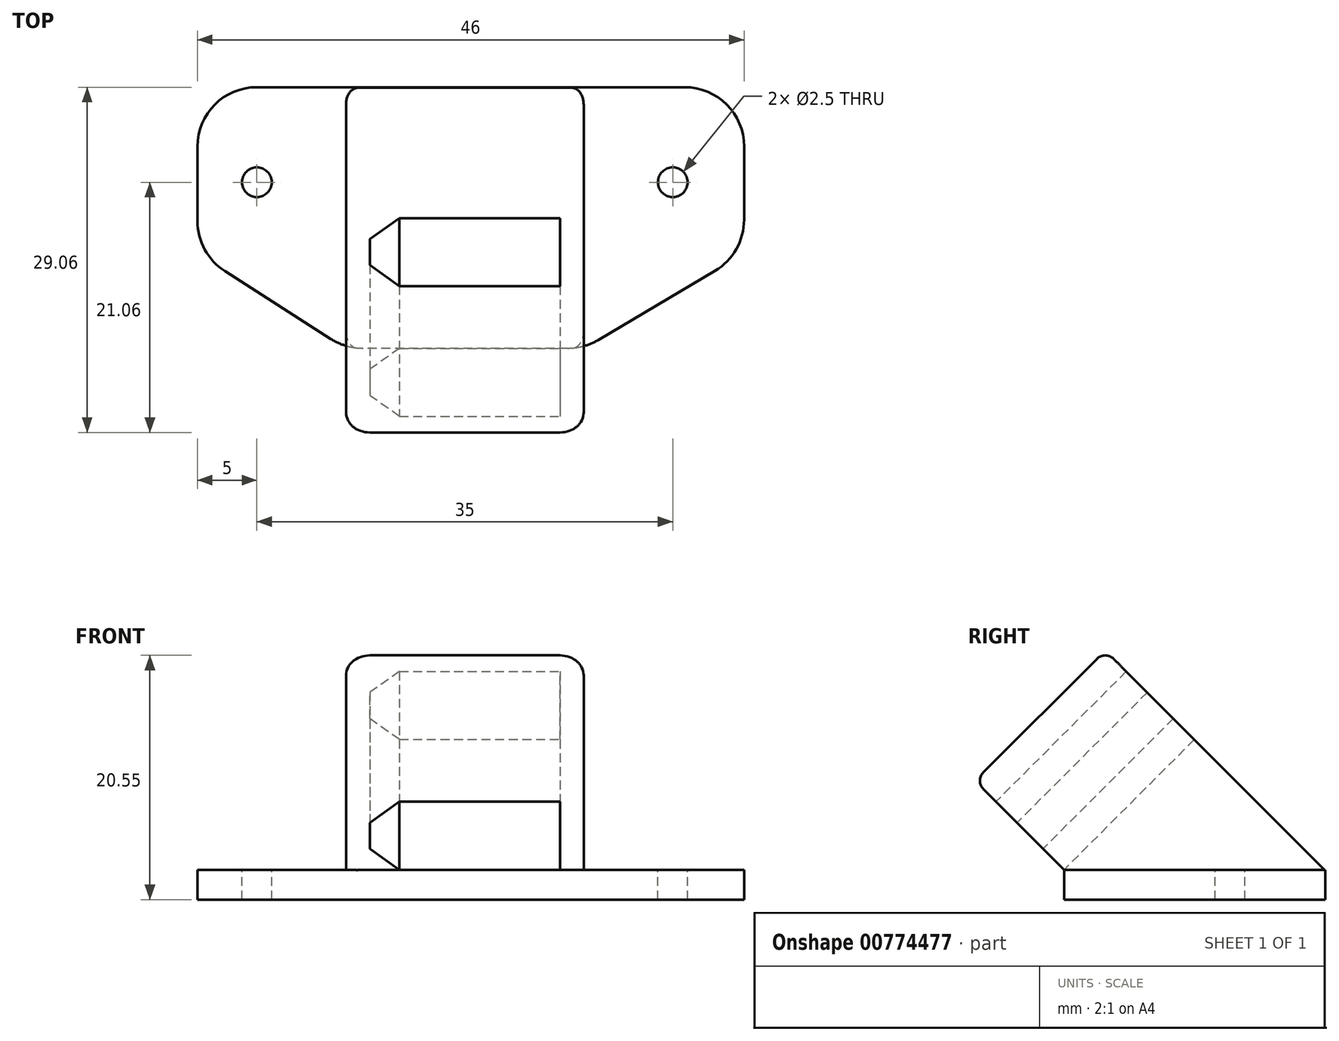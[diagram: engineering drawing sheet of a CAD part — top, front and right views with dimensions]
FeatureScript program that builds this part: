
annotation { "Feature Type Name" : "Feature", "Feature Type Description" : "" }
export const myFeature = defineFeature(function(context is Context, id is Id, definition is map)
    precondition{}
    {
        {
            var Q0;
            Q0=qCreatedBy(makeId("Top.planeOp"),FACE);
            var sketch = newSketch(context, id + "F0", { "sketchPlane" : qUnion([Q0])});
            skLineSegment(sketch, "E0.bottom", {"start": v(-22.5, -7.5) * mm, "end": v(23.5, -7.5) * mm});
            skLineSegment(sketch, "E0.top", {"start": v(-22.5, -29.5) * mm, "end": v(23.5, -29.5) * mm});
            skLineSegment(sketch, "E0.left", {"start": v(-22.5, -7.5) * mm, "end": v(-22.5, -29.5) * mm});
            skLineSegment(sketch, "E0.right", {"start": v(23.5, -7.5) * mm, "end": v(23.5, -29.5) * mm});
            skCircle(sketch, "E1", {"center": v(-17.5, -15.5) * mm, "radius": 1.25 * mm});
            skPoint(sketch, "E1.centerSnap0", {"position": v(-22.5, -15.5) * mm});
            skCircle(sketch, "E2.MirrorC", {"center": v(17.5, -15.5) * mm, "radius": 1.25 * mm});
            skLineSegment(sketch, "E3", {"start": v(-22.5, -21.5) * mm, "end": v(-10, -29.5) * mm});
            skLineSegment(sketch, "E4", {"start": v(23.5, -21.5) * mm, "end": v(10, -29.5) * mm});
            skSolve(sketch);
        }
        {
            var Q0;
            Q0=makeQuery(id+"F0.imprint","IMPRINT",FACE,{"disambiguationData":[TD([[makeQuery(id+"F0.imprint","IMPRINT",EDGE,{"derivedFrom":sQuery(id+"F0.wireOp",EDGE,"E0.bottom")}),-1.0]])]});
            extrude(context, id + "F1", {"entities" : qUnion([Q0]), "oppositeDirection" : true, "depth" : 2.5 * mm, "offsetDistance" : 25 * mm});
        }
        {
            var Q0;
            Q0=qCreatedBy(makeId("Top.planeOp"),FACE);
            var sketch = newSketch(context, id + "F2", { "sketchPlane" : qUnion([Q0])});
            skLineSegment(sketch, "E5.bottom", {"start": v(-10, 0) * mm, "end": v(10, 0) * mm});
            skLineSegment(sketch, "E5.top", {"start": v(-10, 15.5) * mm, "end": v(10, 15.5) * mm});
            skLineSegment(sketch, "E5.left", {"start": v(-10, 0) * mm, "end": v(-10, 15.5) * mm});
            skLineSegment(sketch, "E5.right", {"start": v(10, 0) * mm, "end": v(10, 15.5) * mm});
            skSolve(sketch);
        }
        {
            var Q0;
            Q0 = qSketchRegion(id + "F2", true);
            extrude(context, id + "F3", {"entities" : qUnion([Q0]), "operationType" : NewBodyOperationType.ADD, "depth" : 27 * mm, "offsetDistance" : 25 * mm});
        }
        {
            var Q0;
            Q0=makeQuery(id+"F3.opExtrude","SWEPT_FACE",FACE,{"disambiguationData":[OSD([sQuery(id+"F2.wireOp",EDGE,"E5.bottom")])]});
            var sketch = newSketch(context, id + "F4", { "sketchPlane" : qUnion([Q0])});
            skLineSegment(sketch, "E6.bottom", {"start": v(-8, 24.5) * mm, "end": v(8, 24.5) * mm});
            skLineSegment(sketch, "E6.top", {"start": v(-8, 16.4) * mm, "end": v(8, 16.4) * mm});
            skLineSegment(sketch, "E6.left", {"start": v(8, 16.4) * mm, "end": v(8, 24.5) * mm});
            skLineSegment(sketch, "E6.right", {"start": v(-8, 16.4) * mm, "end": v(-8, 24.5) * mm});
            skLineSegment(sketch, "E7", {"start": v(-5.5, 24.5) * mm, "end": v(-8, 22) * mm});
            skLineSegment(sketch, "E8", {"start": v(-5.5, 16.4) * mm, "end": v(-8, 18.9) * mm});
            skSolve(sketch);
        }
        {
            var Q0;
            {var subQ3=sQuery(id+"F4.wireOp",EDGE,"E6.left");Q0=makeQuery(id+"F4.imprint","IMPRINT",FACE,{"disambiguationData":[TD([[makeQuery(id+"F4.imprint","IMPRINT",EDGE,{"derivedFrom":subQ3}),1.0]])]});}
            var Q1;
            Q1=makeQuery(id+"F3.opExtrude","SWEPT_FACE",FACE,{"disambiguationData":[OSD([sQuery(id+"F2.wireOp",EDGE,"E5.top")])]});
            extrude(context, id + "F5", {"entities" : qUnion([Q0]), "operationType" : NewBodyOperationType.REMOVE, "endBound" : BoundingType.UP_TO_SURFACE, "oppositeDirection" : true, "depth" : 25 * mm, "endBoundEntityFace" : qUnion([Q1]), "offsetDistance" : 25 * mm});
        }
        {
            var Q0;
            Q0=qCreatedBy(makeId("Top.planeOp"),FACE);
            var sketch = newSketch(context, id + "F6", { "sketchPlane" : qUnion([Q0])});
            skLineSegment(sketch, "E9", {"start": v(-27.41, 0) * mm, "end": v(24.32, 0) * mm, "construction": true});
            skSolve(sketch);
        }
        {
            var Q0;
            Q0=makeQuery(id+"F3.opExtrude","SWEPT_BODY",BODY,{"disambiguationData":[OSD([sQuery(id+"F2.wireOp",EDGE,"E5.bottom"),sQuery(id+"F2.wireOp",EDGE,"E5.top"),sQuery(id+"F2.wireOp",EDGE,"E5.left"),sQuery(id+"F2.wireOp",EDGE,"E5.right")])]});
            var Q1;
            Q1=sQuery(id+"F6.wireOp",EDGE,"E9");
            transform(context, id + "F7", {"entities" : qUnion([Q0]), "transformType" : TransformType.ROTATION, "transformAxis" : qUnion([Q1]), "angle" : 45 * degree, "makeCopy" : false});
        }
        {
            var Q0;
            Q0=makeQuery(id+"F3.opExtrude","SWEPT_BODY",BODY,{"disambiguationData":[OSD([sQuery(id+"F2.wireOp",EDGE,"E5.bottom"),sQuery(id+"F2.wireOp",EDGE,"E5.top"),sQuery(id+"F2.wireOp",EDGE,"E5.left"),sQuery(id+"F2.wireOp",EDGE,"E5.right")])]});
            transform(context, id + "F8", {"entities" : qUnion([Q0]), "transformType" : TransformType.TRANSLATION_3D, "dx" : 0 * mm, "dy" : -17.88 * mm, "dz" : -11.6 * mm, "makeCopy" : false});
        }
        {
            var Q0;
            Q0=makeQuery(id+"F1.opExtrude","SWEPT_BODY",BODY,{"disambiguationData":[OSD([sQuery(id+"F0.wireOp",EDGE,"E0.bottom"),sQuery(id+"F0.wireOp",EDGE,"E0.top"),sQuery(id+"F0.wireOp",EDGE,"E0.left"),sQuery(id+"F0.wireOp",EDGE,"E0.right"),sQuery(id+"F0.wireOp",EDGE,"E1"),sQuery(id+"F0.wireOp",EDGE,"E2.MirrorC")])]});
            var Q1;
            Q1=makeQuery(id+"F3.opExtrude","SWEPT_BODY",BODY,{"disambiguationData":[OSD([sQuery(id+"F2.wireOp",EDGE,"E5.bottom"),sQuery(id+"F2.wireOp",EDGE,"E5.top"),sQuery(id+"F2.wireOp",EDGE,"E5.left"),sQuery(id+"F2.wireOp",EDGE,"E5.right")])]});
            booleanBodies(context, id + "F9", {"operationType" : BooleanOperationType.UNION, "tools" : qUnion([Q0, Q1])});
        }
        {
            var Q0;
            Q0=qCreatedBy(makeId("Right.planeOp"),FACE);
            var sketch = newSketch(context, id + "F10", { "sketchPlane" : qUnion([Q0])});
            skLineSegment(sketch, "E10", {"start": v(-36.97, 7.5) * mm, "end": v(-29.47, 0) * mm});
            skLineSegment(sketch, "E11", {"start": v(-29.47, -2.5) * mm, "end": v(-7.5, -2.5) * mm});
            skLineSegment(sketch, "E12", {"start": v(-7.5, -2.5) * mm, "end": v(-7.5, 0) * mm});
            skLineSegment(sketch, "E13", {"start": v(-7.5, 0) * mm, "end": v(-5.54, 0) * mm});
            skLineSegment(sketch, "E14", {"start": v(-5.54, 0) * mm, "end": v(-5.54, -13.55) * mm});
            skLineSegment(sketch, "E15", {"start": v(-5.54, -13.55) * mm, "end": v(-36.97, -13.55) * mm});
            skLineSegment(sketch, "E16", {"start": v(-36.97, -13.55) * mm, "end": v(-36.97, 7.5) * mm});
            skLineSegment(sketch, "E17", {"start": v(-29.47, 0) * mm, "end": v(-29.47, -2.5) * mm});
            skSolve(sketch);
        }
        {
            var Q0;
            Q0=makeQuery(id+"F10.imprint","IMPRINT",FACE,{"disambiguationData":[TD([[makeQuery(id+"F10.imprint","IMPRINT",EDGE,{"derivedFrom":sQuery(id+"F10.wireOp",EDGE,"E10")}),-1.0]])]});
            extrude(context, id + "F11", {"entities" : qUnion([Q0]), "operationType" : NewBodyOperationType.REMOVE, "endBound" : BoundingType.SYMMETRIC, "depth" : 50 * mm, "offsetDistance" : 25 * mm});
        }
        {
            var Q0;
            Q0=makeQuery(id+"F3.opExtrude","CAP_EDGE",EDGE,{"disambiguationData":[OSD([sQuery(id+"F2.wireOp",EDGE,"E5.left")])],"isStart":false});
            var Q1;
            Q1=makeQuery(id+"F3.opExtrude","CAP_EDGE",EDGE,{"disambiguationData":[OSD([sQuery(id+"F2.wireOp",EDGE,"E5.right")])],"isStart":false});
            fillet(context, id + "F12", {"entities" : qUnion([Q0, Q1]), "radius" : 2 * mm, "tangentPropagation" : true, "allowEdgeOverflow" : false});
        }
        {
            var Q0;
            {var subQ0=sQuery(id+"F2.wireOp",EDGE,"E5.top");var subQ1=sQuery(id+"F2.wireOp",EDGE,"E5.left");Q0=makeQuery(id+"F9.opBoolean","SPLIT",EDGE,{"disambiguationData":[TD([makeQuery(id+"F3.opExtrude","CAP_FACE",FACE,{"disambiguationData":[OSD([sQuery(id+"F2.wireOp",EDGE,"E5.bottom"),subQ0,subQ1,sQuery(id+"F2.wireOp",EDGE,"E5.right")])],"isStart":false})])],"derivedFrom":makeQuery(id+"F3.opExtrude","SWEPT_EDGE",EDGE,{"disambiguationData":[OSD([subQ0,subQ1])]})});}
            var Q1;
            Q1=makeQuery(id+"F3.opExtrude","CAP_EDGE",EDGE,{"disambiguationData":[OSD([sQuery(id+"F2.wireOp",EDGE,"E5.top")])],"isStart":false});
            var Q2;
            {var subQ0=sQuery(id+"F2.wireOp",EDGE,"E5.top");var subQ1=sQuery(id+"F2.wireOp",EDGE,"E5.right");Q2=makeQuery(id+"F9.opBoolean","SPLIT",EDGE,{"disambiguationData":[TD([makeQuery(id+"F3.opExtrude","CAP_FACE",FACE,{"disambiguationData":[OSD([sQuery(id+"F2.wireOp",EDGE,"E5.bottom"),subQ0,sQuery(id+"F2.wireOp",EDGE,"E5.left"),subQ1])],"isStart":false})])],"derivedFrom":makeQuery(id+"F3.opExtrude","SWEPT_EDGE",EDGE,{"disambiguationData":[OSD([subQ0,subQ1])]})});}
            var Q3;
            Q3=makeQuery(id+"F3.opExtrude","CAP_EDGE",EDGE,{"disambiguationData":[OSD([sQuery(id+"F2.wireOp",EDGE,"E5.bottom")])],"isStart":false});
            fillet(context, id + "F13", {"entities" : qUnion([Q0, Q1, Q2, Q3]), "radius" : 1 * mm, "tangentPropagation" : true, "allowEdgeOverflow" : false});
        }
        {
            var Q0;
            Q0=makeQuery(id+"F1.opExtrude","SWEPT_EDGE",EDGE,{"disambiguationData":[OSD([sQuery(id+"F0.wireOp",EDGE,"E0.left"),sQuery(id+"F0.wireOp",EDGE,"E3")])]});
            var Q1;
            Q1=makeQuery(id+"F1.opExtrude","SWEPT_EDGE",EDGE,{"disambiguationData":[OSD([sQuery(id+"F0.wireOp",EDGE,"E0.bottom"),sQuery(id+"F0.wireOp",EDGE,"E0.left")])]});
            var Q2;
            Q2=makeQuery(id+"F1.opExtrude","SWEPT_EDGE",EDGE,{"disambiguationData":[OSD([sQuery(id+"F0.wireOp",EDGE,"E0.bottom"),sQuery(id+"F0.wireOp",EDGE,"E0.right")])]});
            var Q3;
            Q3=makeQuery(id+"F1.opExtrude","SWEPT_EDGE",EDGE,{"disambiguationData":[OSD([sQuery(id+"F0.wireOp",EDGE,"E0.right"),sQuery(id+"F0.wireOp",EDGE,"E4")])]});
            var Q4;
            Q4=makeQuery(id+"F11.boolean.opBoolean","INTERSECT",EDGE,{"derivedFrom":[makeQuery(id+"F1.opExtrude","SWEPT_FACE",FACE,{"disambiguationData":[OSD([sQuery(id+"F0.wireOp",EDGE,"E3")])]}),makeQuery(id+"F11.opExtrude","SWEPT_FACE",FACE,{"disambiguationData":[OSD([sQuery(id+"F10.wireOp",EDGE,"E17")])]})]});
            var Q5;
            Q5=makeQuery(id+"F11.boolean.opBoolean","INTERSECT",EDGE,{"derivedFrom":[makeQuery(id+"F1.opExtrude","SWEPT_FACE",FACE,{"disambiguationData":[OSD([sQuery(id+"F0.wireOp",EDGE,"E4")])]}),makeQuery(id+"F11.opExtrude","SWEPT_FACE",FACE,{"disambiguationData":[OSD([sQuery(id+"F10.wireOp",EDGE,"E17")])]})]});
            fillet(context, id + "F14", {"entities" : qUnion([Q0, Q1, Q2, Q3, Q4, Q5]), "radius" : 5 * mm, "tangentPropagation" : true, "allowEdgeOverflow" : false});
        }
    });
